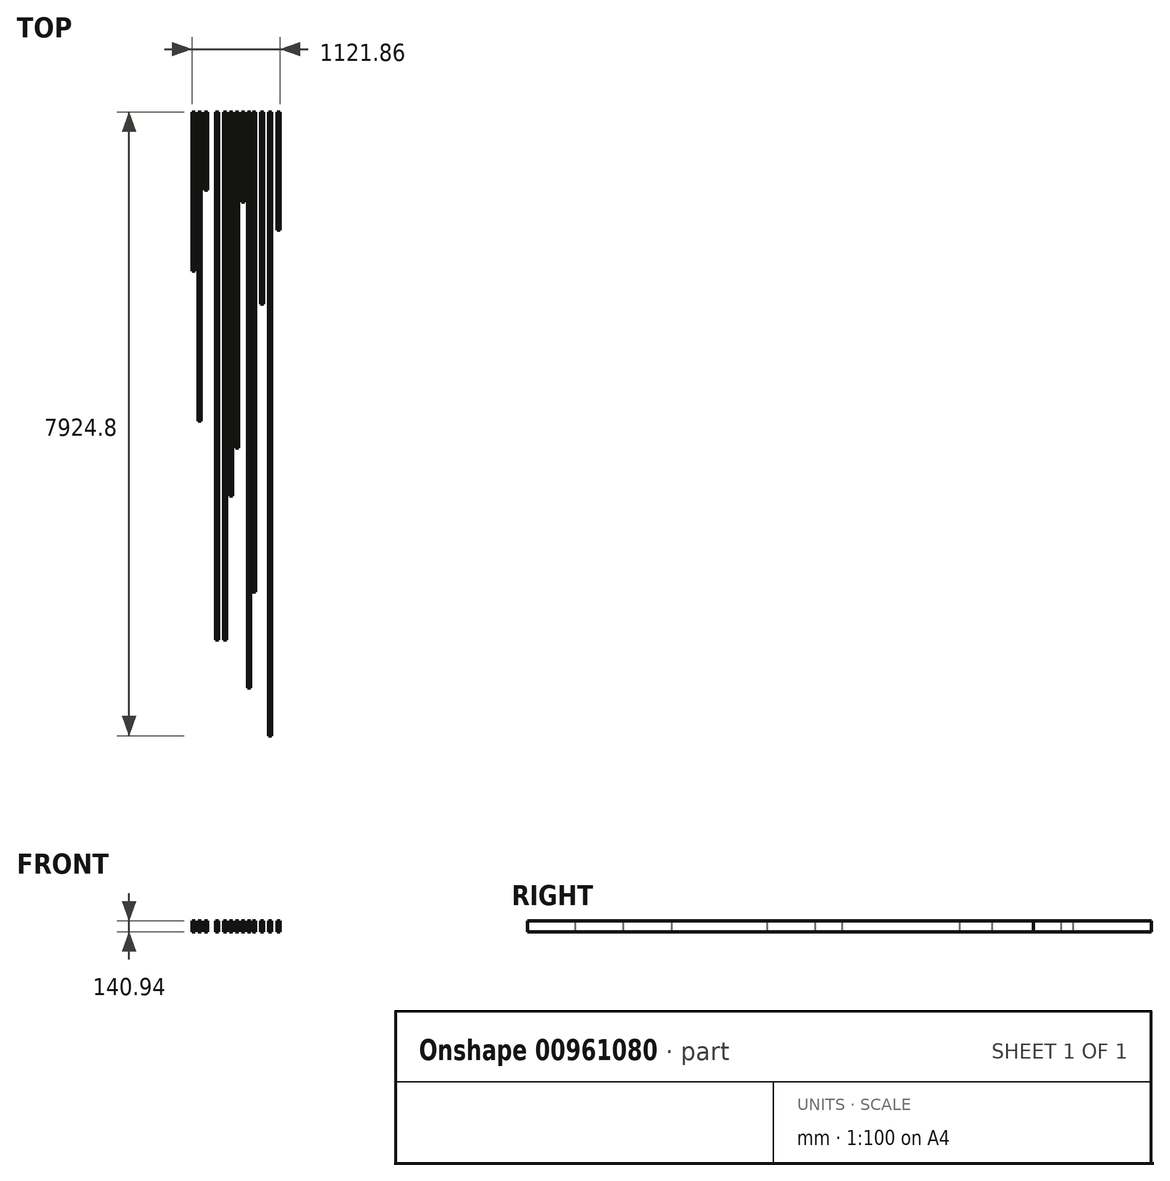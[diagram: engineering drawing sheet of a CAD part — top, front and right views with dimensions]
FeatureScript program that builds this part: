
annotation { "Feature Type Name" : "Feature", "Feature Type Description" : "" }
export const myFeature = defineFeature(function(context is Context, id is Id, definition is map)
    precondition{}
    {
        {
            var Q0;
            Q0=qCreatedBy(makeId("Front.planeOp"),FACE);
            var sketch = newSketch(context, id + "F0", { "sketchPlane" : qUnion([Q0])});
            skLineSegment(sketch, "E0.bottom", {"start": v(19.05, -69.85) * mm, "end": v(-19.05, -69.85) * mm});
            skLineSegment(sketch, "E0.top", {"start": v(19.05, 69.85) * mm, "end": v(-19.05, 69.85) * mm});
            skLineSegment(sketch, "E0.left", {"start": v(19.05, -69.85) * mm, "end": v(19.05, 69.85) * mm});
            skLineSegment(sketch, "E0.right", {"start": v(-19.05, -69.85) * mm, "end": v(-19.05, 69.85) * mm});
            skPoint(sketch, "E0.middle", {"position": v(0, 0) * mm});
            skLineSegment(sketch, "E1.1.0.0", {"start": v(57.15, -69.85) * mm, "end": v(57.15, 69.85) * mm});
            skLineSegment(sketch, "E1.1.0.1", {"start": v(95.25, 69.85) * mm, "end": v(57.15, 69.85) * mm});
            skLineSegment(sketch, "E1.1.0.2", {"start": v(95.25, -69.85) * mm, "end": v(95.25, 69.85) * mm});
            skLineSegment(sketch, "E1.1.0.3", {"start": v(95.25, -69.85) * mm, "end": v(57.15, -69.85) * mm});
            skLineSegment(sketch, "E1.2.0.0", {"start": v(133.35, -69.85) * mm, "end": v(133.35, 69.85) * mm});
            skLineSegment(sketch, "E1.2.0.1", {"start": v(171.45, 69.85) * mm, "end": v(133.35, 69.85) * mm});
            skLineSegment(sketch, "E1.2.0.2", {"start": v(171.45, -69.85) * mm, "end": v(171.45, 69.85) * mm});
            skLineSegment(sketch, "E1.2.0.3", {"start": v(171.45, -69.85) * mm, "end": v(133.35, -69.85) * mm});
            skLineSegment(sketch, "E1.direction1", {"start": v(-19.05, -69.85) * mm, "end": v(57.15, -69.85) * mm, "construction": true});
            skLineSegment(sketch, "E2.0.3.0", {"start": v(209.55, -69.85) * mm, "end": v(209.55, 69.85) * mm});
            skLineSegment(sketch, "E2.3.3.0", {"start": v(247.65, 69.85) * mm, "end": v(209.55, 69.85) * mm});
            skLineSegment(sketch, "E2.6.3.0", {"start": v(247.65, -69.85) * mm, "end": v(247.65, 69.85) * mm});
            skLineSegment(sketch, "E2.9.3.0", {"start": v(247.65, -69.85) * mm, "end": v(209.55, -69.85) * mm});
            skLineSegment(sketch, "E2.0.4.0", {"start": v(285.75, -69.85) * mm, "end": v(285.75, 69.85) * mm});
            skLineSegment(sketch, "E2.3.4.0", {"start": v(323.85, 69.85) * mm, "end": v(285.75, 69.85) * mm});
            skLineSegment(sketch, "E2.6.4.0", {"start": v(323.85, -69.85) * mm, "end": v(323.85, 69.85) * mm});
            skLineSegment(sketch, "E2.9.4.0", {"start": v(323.85, -69.85) * mm, "end": v(285.75, -69.85) * mm});
            skLineSegment(sketch, "E3.bottom", {"start": v(346.6, 70.57) * mm, "end": v(384.7, 70.57) * mm});
            skLineSegment(sketch, "E3.top", {"start": v(346.6, -69.13) * mm, "end": v(384.7, -69.13) * mm});
            skLineSegment(sketch, "E3.left", {"start": v(346.6, 70.57) * mm, "end": v(346.6, -69.13) * mm});
            skLineSegment(sketch, "E3.right", {"start": v(384.7, 70.57) * mm, "end": v(384.7, -69.13) * mm});
            skLineSegment(sketch, "E4.bottom", {"start": v(451.71, 70.32) * mm, "end": v(489.81, 70.32) * mm});
            skLineSegment(sketch, "E4.top", {"start": v(451.71, -69.38) * mm, "end": v(489.81, -69.38) * mm});
            skLineSegment(sketch, "E4.left", {"start": v(451.71, 70.32) * mm, "end": v(451.71, -69.38) * mm});
            skLineSegment(sketch, "E4.right", {"start": v(489.81, 70.32) * mm, "end": v(489.81, -69.38) * mm});
            skLineSegment(sketch, "E5.bottom", {"start": v(549.7, 70.57) * mm, "end": v(587.8, 70.57) * mm});
            skLineSegment(sketch, "E5.top", {"start": v(549.7, -69.13) * mm, "end": v(587.8, -69.13) * mm});
            skLineSegment(sketch, "E5.left", {"start": v(549.7, 70.57) * mm, "end": v(549.7, -69.13) * mm});
            skLineSegment(sketch, "E5.right", {"start": v(587.8, 70.57) * mm, "end": v(587.8, -69.13) * mm});
            skLineSegment(sketch, "E6.bottom", {"start": v(662.41, 70.57) * mm, "end": v(700.51, 70.57) * mm});
            skLineSegment(sketch, "E6.top", {"start": v(662.41, -69.13) * mm, "end": v(700.51, -69.13) * mm});
            skLineSegment(sketch, "E6.left", {"start": v(662.41, 70.57) * mm, "end": v(662.41, -69.13) * mm});
            skLineSegment(sketch, "E6.right", {"start": v(700.51, 70.57) * mm, "end": v(700.51, -69.13) * mm});
            skLineSegment(sketch, "E7.2.0.0", {"start": v(-146.26, -71.8) * mm, "end": v(-146.26, 67.9) * mm});
            skLineSegment(sketch, "E7.2.0.1", {"start": v(-108.16, 67.9) * mm, "end": v(-146.26, 67.9) * mm});
            skLineSegment(sketch, "E7.2.0.2", {"start": v(-108.16, -71.8) * mm, "end": v(-108.16, 67.9) * mm});
            skLineSegment(sketch, "E7.2.0.3", {"start": v(-108.16, -71.8) * mm, "end": v(-146.26, -71.8) * mm});
            skLineSegment(sketch, "E8.2.0.0", {"start": v(-259.79, -68.6) * mm, "end": v(-259.79, 71.1) * mm});
            skLineSegment(sketch, "E8.2.0.1", {"start": v(-221.69, 71.1) * mm, "end": v(-259.79, 71.1) * mm});
            skLineSegment(sketch, "E8.2.0.2", {"start": v(-221.69, -68.6) * mm, "end": v(-221.69, 71.1) * mm});
            skLineSegment(sketch, "E8.2.0.3", {"start": v(-221.69, -68.6) * mm, "end": v(-259.79, -68.6) * mm});
            skLineSegment(sketch, "E9.2.0.0", {"start": v(-346.06, -68.6) * mm, "end": v(-346.06, 71.1) * mm});
            skLineSegment(sketch, "E9.2.0.1", {"start": v(-307.96, 71.1) * mm, "end": v(-346.06, 71.1) * mm});
            skLineSegment(sketch, "E9.2.0.2", {"start": v(-307.96, -68.6) * mm, "end": v(-307.96, 71.1) * mm});
            skLineSegment(sketch, "E9.2.0.3", {"start": v(-307.96, -68.6) * mm, "end": v(-346.06, -68.6) * mm});
            skLineSegment(sketch, "E10.2.0.0", {"start": v(-421.35, -69.13) * mm, "end": v(-421.35, 70.57) * mm});
            skLineSegment(sketch, "E10.2.0.1", {"start": v(-383.25, 70.57) * mm, "end": v(-421.35, 70.57) * mm});
            skLineSegment(sketch, "E10.2.0.2", {"start": v(-383.25, -69.13) * mm, "end": v(-383.25, 70.57) * mm});
            skLineSegment(sketch, "E10.2.0.3", {"start": v(-383.25, -69.13) * mm, "end": v(-421.35, -69.13) * mm});
            skSolve(sketch);
        }
        {
            var Q0;
            Q0=makeQuery(id+"F0.imprint","IMPRINT",FACE,{"disambiguationData":[TD([[makeQuery(id+"F0.imprint","IMPRINT",EDGE,{"derivedFrom":sQuery(id+"F0.wireOp",EDGE,"E0.bottom")}),-1.0]])]});
            extrude(context, id + "F1", {"entities" : qUnion([Q0]), "depth" : 6705.6 * mm, "offsetDistance" : 25.4 * mm});
        }
        {
            var Q0;
            Q0=makeQuery(id+"F0.imprint","IMPRINT",FACE,{"disambiguationData":[TD([[makeQuery(id+"F0.imprint","IMPRINT",EDGE,{"derivedFrom":sQuery(id+"F0.wireOp",EDGE,"E1.1.0.0")}),-1.0]])]});
            extrude(context, id + "F2", {"entities" : qUnion([Q0]), "depth" : 4876.8 * mm, "offsetDistance" : 25.4 * mm});
        }
        {
            var Q0;
            Q0=makeQuery(id+"F0.imprint","IMPRINT",FACE,{"disambiguationData":[TD([[makeQuery(id+"F0.imprint","IMPRINT",EDGE,{"derivedFrom":sQuery(id+"F0.wireOp",EDGE,"E1.2.0.0")}),-1.0]])]});
            extrude(context, id + "F3", {"entities" : qUnion([Q0]), "depth" : 4267.2 * mm, "offsetDistance" : 25.4 * mm});
        }
        {
            var Q0;
            Q0=makeQuery(id+"F0.imprint","IMPRINT",FACE,{"disambiguationData":[TD([[makeQuery(id+"F0.imprint","IMPRINT",EDGE,{"derivedFrom":sQuery(id+"F0.wireOp",EDGE,"E2.0.3.0")}),-1.0]])]});
            extrude(context, id + "F4", {"entities" : qUnion([Q0]), "depth" : 1143 * mm, "offsetDistance" : 25.4 * mm});
        }
        {
            var Q0;
            Q0=makeQuery(id+"F1.opExtrude","SWEPT_BODY",BODY,{"disambiguationData":[OSD([sQuery(id+"F0.wireOp",EDGE,"E0.bottom"),sQuery(id+"F0.wireOp",EDGE,"E0.top"),sQuery(id+"F0.wireOp",EDGE,"E0.left"),sQuery(id+"F0.wireOp",EDGE,"E0.right")])]});
            transform(context, id + "F5", {"entities" : qUnion([Q0]), "transformType" : TransformType.TRANSLATION_3D, "dx" : -101.6 * mm, "dy" : 0 * mm, "dz" : 0 * mm, "makeCopy" : true});
        }
        {
            var Q0;
            Q0=makeQuery(id+"F0.imprint","IMPRINT",FACE,{"disambiguationData":[TD([[makeQuery(id+"F0.imprint","IMPRINT",EDGE,{"derivedFrom":sQuery(id+"F0.wireOp",EDGE,"E2.0.4.0")}),-1.0]])]});
            extrude(context, id + "F6", {"entities" : qUnion([Q0]), "depth" : 7315.2 * mm, "offsetDistance" : 25.4 * mm});
        }
        {
            var Q0;
            Q0=makeQuery(id+"F0.imprint","IMPRINT",FACE,{"disambiguationData":[TD([[makeQuery(id+"F0.imprint","IMPRINT",EDGE,{"derivedFrom":sQuery(id+"F0.wireOp",EDGE,"E3.bottom")}),-1.0]])]});
            extrude(context, id + "F7", {"entities" : qUnion([Q0]), "depth" : 6096 * mm, "offsetDistance" : 25.4 * mm});
        }
        {
            var Q0;
            Q0=makeQuery(id+"F0.imprint","IMPRINT",FACE,{"disambiguationData":[TD([[makeQuery(id+"F0.imprint","IMPRINT",EDGE,{"derivedFrom":sQuery(id+"F0.wireOp",EDGE,"E4.bottom")}),-1.0]])]});
            extrude(context, id + "F8", {"entities" : qUnion([Q0]), "depth" : 2438.4 * mm, "offsetDistance" : 25.4 * mm});
        }
        {
            var Q0;
            Q0=makeQuery(id+"F0.imprint","IMPRINT",FACE,{"disambiguationData":[TD([[makeQuery(id+"F0.imprint","IMPRINT",EDGE,{"derivedFrom":sQuery(id+"F0.wireOp",EDGE,"E5.bottom")}),-1.0]])]});
            extrude(context, id + "F9", {"entities" : qUnion([Q0]), "depth" : 7924.8 * mm, "offsetDistance" : 25.4 * mm});
        }
        {
            var Q0;
            Q0=makeQuery(id+"F0.imprint","IMPRINT",FACE,{"disambiguationData":[TD([[makeQuery(id+"F0.imprint","IMPRINT",EDGE,{"derivedFrom":sQuery(id+"F0.wireOp",EDGE,"E6.bottom")}),-1.0]])]});
            extrude(context, id + "F10", {"entities" : qUnion([Q0]), "depth" : 1498.6 * mm, "offsetDistance" : 25.4 * mm});
        }
        {
            var Q0;
            Q0=makeQuery(id+"F0.imprint","IMPRINT",FACE,{"disambiguationData":[TD([[makeQuery(id+"F0.imprint","IMPRINT",EDGE,{"derivedFrom":sQuery(id+"F0.wireOp",EDGE,"E8.2.0.0")}),-1.0]])]});
            extrude(context, id + "F11", {"entities" : qUnion([Q0]), "depth" : 990.6 * mm, "offsetDistance" : 25.4 * mm});
        }
        {
            var Q0;
            Q0=makeQuery(id+"F0.imprint","IMPRINT",FACE,{"disambiguationData":[TD([[makeQuery(id+"F0.imprint","IMPRINT",EDGE,{"derivedFrom":sQuery(id+"F0.wireOp",EDGE,"E9.2.0.0")}),-1.0]])]});
            extrude(context, id + "F12", {"entities" : qUnion([Q0]), "depth" : 3924.3 * mm, "offsetDistance" : 25.4 * mm});
        }
        {
            var Q0;
            Q0=makeQuery(id+"F0.imprint","IMPRINT",FACE,{"disambiguationData":[TD([[makeQuery(id+"F0.imprint","IMPRINT",EDGE,{"derivedFrom":sQuery(id+"F0.wireOp",EDGE,"E10.2.0.0")}),-1.0]])]});
            extrude(context, id + "F13", {"entities" : qUnion([Q0]), "depth" : 2019.3 * mm, "offsetDistance" : 25.4 * mm});
        }
    });
